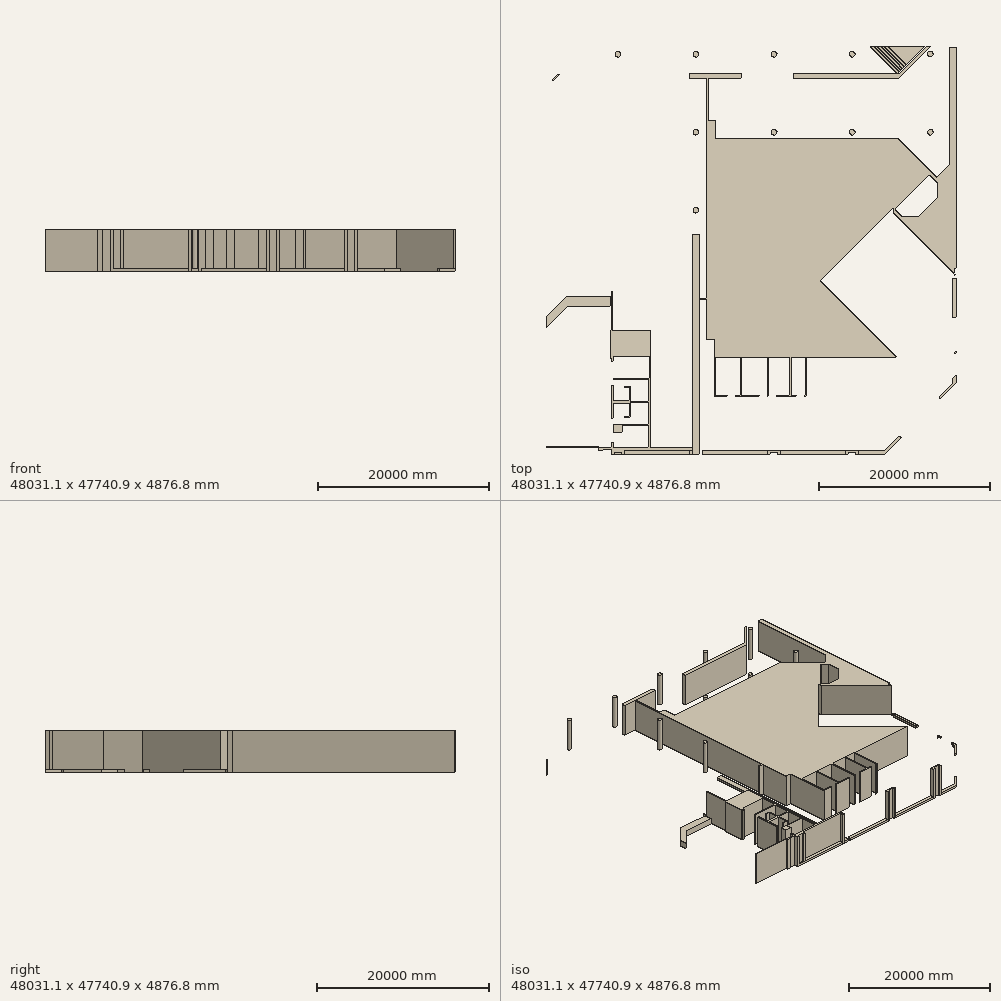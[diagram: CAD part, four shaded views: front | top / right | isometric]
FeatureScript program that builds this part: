
annotation { "Feature Type Name" : "Feature", "Feature Type Description" : "" }
export const myFeature = defineFeature(function(context is Context, id is Id, definition is map)
    precondition{}
    {
        {
            var Q0;
            Q0=qCreatedBy(makeId("Top.planeOp"),FACE);
            var sketch = newSketch(context, id + "F0", { "sketchPlane" : qUnion([Q0])});
            skPoint(sketch, "E0", {"position": v(-26.85, 4562) * mm});
            skPoint(sketch, "E1", {"position": v(-26.85, -4582) * mm});
            skLineSegment(sketch, "E2", {"start": v(-9950.22, -31763.64) * mm, "end": v(-9950.22, -33159.86) * mm});
            skLineSegment(sketch, "E3.bottom", {"start": v(-17558.31, -32264.25) * mm, "end": v(-11455.84, -32264.25) * mm});
            skLineSegment(sketch, "E3.top", {"start": v(-17558.31, -32382.5) * mm, "end": v(-11455.84, -32382.5) * mm});
            skLineSegment(sketch, "E3.left", {"start": v(-17558.31, -32264.25) * mm, "end": v(-17558.31, -32382.5) * mm});
            skLineSegment(sketch, "E3.right", {"start": v(-11455.84, -32264.25) * mm, "end": v(-11455.84, -32382.5) * mm});
            skLineSegment(sketch, "E4.bottom", {"start": v(-11455.84, -32382.5) * mm, "end": v(-10938.34, -32382.5) * mm});
            skLineSegment(sketch, "E4.top", {"start": v(-11455.84, -32680.38) * mm, "end": v(-10938.34, -32680.38) * mm});
            skLineSegment(sketch, "E4.left", {"start": v(-11455.84, -32382.5) * mm, "end": v(-11455.84, -32680.38) * mm});
            skLineSegment(sketch, "E4.right", {"start": v(-10938.34, -32382.5) * mm, "end": v(-10938.34, -32680.38) * mm});
            skLineSegment(sketch, "E5", {"start": v(-9950.22, -31763.64) * mm, "end": v(-9762.7, -31763.64) * mm});
            skLineSegment(sketch, "E6", {"start": v(-9762.7, -31763.64) * mm, "end": v(-9762.7, -32380.3) * mm});
            skLineSegment(sketch, "E7", {"start": v(-9762.7, -32380.3) * mm, "end": v(-5641.05, -32380.3) * mm});
            skLineSegment(sketch, "E8", {"start": v(-9950.22, -33159.86) * mm, "end": v(-9619.14, -33159.86) * mm});
            skLineSegment(sketch, "E9", {"start": v(-9619.14, -33159.86) * mm, "end": v(-9619.14, -32907.45) * mm});
            skLineSegment(sketch, "E10", {"start": v(-9619.14, -32907.45) * mm, "end": v(-8738.2, -32907.45) * mm});
            skLineSegment(sketch, "E11", {"start": v(-8738.2, -32907.45) * mm, "end": v(-8738.2, -33145.54) * mm});
            skLineSegment(sketch, "E12", {"start": v(-8738.2, -33145.54) * mm, "end": v(-8410.82, -33145.54) * mm});
            skLineSegment(sketch, "E13", {"start": v(-8410.82, -33145.54) * mm, "end": v(-8410.82, -32669.36) * mm});
            skLineSegment(sketch, "E14", {"start": v(-8410.82, -32669.36) * mm, "end": v(22197.76, -32669.36) * mm});
            skLineSegment(sketch, "E15", {"start": v(22197.76, -32669.36) * mm, "end": v(23797.54, -31074.11) * mm});
            skLineSegment(sketch, "E16", {"start": v(23797.54, -31074.11) * mm, "end": v(24012.82, -31290) * mm});
            skLineSegment(sketch, "E17", {"start": v(24012.82, -31290) * mm, "end": v(26211.2, -31290) * mm});
            skLineSegment(sketch, "E18", {"start": v(26211.2, -31290) * mm, "end": v(28592.14, -28914.34) * mm});
            skLineSegment(sketch, "E19", {"start": v(28592.14, -28914.34) * mm, "end": v(28592.14, -26694.78) * mm});
            skLineSegment(sketch, "E20", {"start": v(28592.14, -26694.78) * mm, "end": v(28388.32, -26490.39) * mm});
            skLineSegment(sketch, "E21", {"start": v(28388.32, -26490.39) * mm, "end": v(30000.29, -24882.99) * mm});
            skLineSegment(sketch, "E22", {"start": v(30000.29, -24882.99) * mm, "end": v(30000.29, -21715.72) * mm});
            skLineSegment(sketch, "E23", {"start": v(30000.29, -21715.72) * mm, "end": v(30471.14, -21715.72) * mm});
            skLineSegment(sketch, "E24", {"start": v(30471.14, -21715.72) * mm, "end": v(30471.14, -21395.8) * mm});
            skLineSegment(sketch, "E25", {"start": v(30471.14, -21395.8) * mm, "end": v(30212.23, -21395.8) * mm});
            skLineSegment(sketch, "E26", {"start": v(30212.23, -21395.8) * mm, "end": v(30212.23, -20478.92) * mm});
            skLineSegment(sketch, "E27", {"start": v(30212.23, -20478.92) * mm, "end": v(30471.14, -20478.92) * mm});
            skPoint(sketch, "E27.endSnap0", {"position": v(30471.14, -21555.76) * mm});
            skLineSegment(sketch, "E28", {"start": v(30471.14, -20478.92) * mm, "end": v(30471.14, -20162.3) * mm});
            skLineSegment(sketch, "E29", {"start": v(30471.14, -20162.3) * mm, "end": v(29991.03, -20162.3) * mm});
            skLineSegment(sketch, "E30", {"start": v(29991.03, -20162.3) * mm, "end": v(30000.29, -12570.11) * mm});
            skLineSegment(sketch, "E31", {"start": v(30000.29, -12570.11) * mm, "end": v(30453.57, -12570.67) * mm});
            skLineSegment(sketch, "E32", {"start": v(30453.57, -12570.67) * mm, "end": v(30453.57, -12236.58) * mm});
            skLineSegment(sketch, "E33", {"start": v(30453.57, -12236.58) * mm, "end": v(30215.9, -12236.58) * mm});
            skLineSegment(sketch, "E34", {"start": v(30215.9, -12236.58) * mm, "end": v(30215.9, -11358.68) * mm});
            skLineSegment(sketch, "E35", {"start": v(30215.9, -11358.68) * mm, "end": v(30472.75, -11358.68) * mm});
            skLineSegment(sketch, "E36", {"start": v(30472.75, -11358.68) * mm, "end": v(30472.75, 14474.16) * mm});
            skLineSegment(sketch, "E37", {"start": v(30472.75, 14474.16) * mm, "end": v(29691.03, 14474.16) * mm});
            skLineSegment(sketch, "E38", {"start": v(29691.03, 14474.16) * mm, "end": v(29691.03, 751.92) * mm});
            skLineSegment(sketch, "E39", {"start": v(29691.03, 751.92) * mm, "end": v(28176.9, -757.92) * mm});
            skLineSegment(sketch, "E40", {"start": v(28176.9, -757.92) * mm, "end": v(27421.13, 0) * mm});
            skLineSegment(sketch, "E41", {"start": v(23102.85, -4306.06) * mm, "end": v(14549.29, -12835.42) * mm});
            skLineSegment(sketch, "E42", {"start": v(23102.85, -4306.06) * mm, "end": v(23102.85, -4877.02) * mm});
            skLineSegment(sketch, "E43", {"start": v(23102.85, -4877.02) * mm, "end": v(36319.55, -18058.09) * mm});
            skLineSegment(sketch, "E44", {"start": v(36319.55, -18058.09) * mm, "end": v(22035.93, -32380.3) * mm});
            skLineSegment(sketch, "E45", {"start": v(23372.41, -4424.26) * mm, "end": v(23372.41, -4562.3) * mm});
            skLineSegment(sketch, "E46", {"start": v(23372.41, -4562.3) * mm, "end": v(24176.25, -5363.97) * mm});
            skLineSegment(sketch, "E47", {"start": v(24176.25, -5363.97) * mm, "end": v(26065.69, -5363.97) * mm});
            skLineSegment(sketch, "E48", {"start": v(26065.69, -5363.97) * mm, "end": v(28200.6, -3235.1) * mm});
            skLineSegment(sketch, "E49", {"start": v(28200.6, -3235.1) * mm, "end": v(28200.6, -1321.07) * mm});
            skLineSegment(sketch, "E50", {"start": v(28200.6, -1321.07) * mm, "end": v(27426.94, -545.21) * mm});
            skLineSegment(sketch, "E51", {"start": v(27426.94, -545.21) * mm, "end": v(27250.2, -545.21) * mm});
            skLineSegment(sketch, "E52", {"start": v(27250.2, -545.21) * mm, "end": v(23372.41, -4424.26) * mm});
            skLineSegment(sketch, "E53", {"start": v(27421.13, 0) * mm, "end": v(23591.37, 3840.63) * mm});
            skLineSegment(sketch, "E54", {"start": v(23591.37, 3840.63) * mm, "end": v(2272.8, 3840.63) * mm});
            skLineSegment(sketch, "E55", {"start": v(2272.8, 3840.63) * mm, "end": v(2272.8, 5998.23) * mm});
            skLineSegment(sketch, "E56", {"start": v(2272.8, 5998.23) * mm, "end": v(1416.9, 5998.23) * mm});
            skLineSegment(sketch, "E57", {"start": v(1416.9, 5998.23) * mm, "end": v(1416.9, 10830.47) * mm});
            skLineSegment(sketch, "E58", {"start": v(1416.9, 10830.47) * mm, "end": v(1221.14, 10830.47) * mm});
            skLineSegment(sketch, "E59", {"start": v(1221.14, 10830.47) * mm, "end": v(1221.14, -14864.76) * mm});
            skLineSegment(sketch, "E60", {"start": v(1221.14, -19710.1) * mm, "end": v(2272.8, -19710.1) * mm});
            skLineSegment(sketch, "E61", {"start": v(2114.71, -20733.64) * mm, "end": v(2114.71, -19710.1) * mm});
            skLineSegment(sketch, "E62", {"start": v(2114.71, -20733.64) * mm, "end": v(2114.71, -26433.55) * mm});
            skLineSegment(sketch, "E63", {"start": v(2114.71, -26433.55) * mm, "end": v(12953.96, -26433.55) * mm});
            skLineSegment(sketch, "E64", {"start": v(12953.96, -26433.55) * mm, "end": v(12953.96, -21846.23) * mm});
            skLineSegment(sketch, "E65", {"start": v(12953.96, -21846.23) * mm, "end": v(23534.6, -21846.23) * mm});
            skLineSegment(sketch, "E66", {"start": v(14549.29, -12835.42) * mm, "end": v(23534.6, -21846.23) * mm});
            skLineSegment(sketch, "E67.bottom", {"start": v(2270.48, -21826.68) * mm, "end": v(5186.94, -21826.68) * mm});
            skLineSegment(sketch, "E67.top", {"start": v(2270.48, -26267.02) * mm, "end": v(5186.94, -26267.02) * mm});
            skLineSegment(sketch, "E67.left", {"start": v(2270.48, -21826.68) * mm, "end": v(2270.48, -26267.02) * mm});
            skLineSegment(sketch, "E67.right", {"start": v(12795.42, -21826.68) * mm, "end": v(12795.42, -26267.02) * mm});
            skLineSegment(sketch, "E68", {"start": v(5186.94, -26267.02) * mm, "end": v(5186.94, -21826.68) * mm});
            skLineSegment(sketch, "E69", {"start": v(5332.87, -21826.68) * mm, "end": v(5332.87, -26267.02) * mm});
            skLineSegment(sketch, "E70", {"start": v(8282.63, -26267.02) * mm, "end": v(8282.63, -21826.68) * mm});
            skLineSegment(sketch, "E71", {"start": v(8448.12, -26267.02) * mm, "end": v(8448.12, -21826.68) * mm});
            skLineSegment(sketch, "E72", {"start": v(10967.35, -26267.02) * mm, "end": v(10967.35, -21826.68) * mm});
            skLineSegment(sketch, "E73", {"start": v(11142.18, -26267.02) * mm, "end": v(11142.18, -21826.68) * mm});
            skLineSegment(sketch, "E74.trimOffspring", {"start": v(5332.87, -26267.02) * mm, "end": v(8282.63, -26267.02) * mm});
            skLineSegment(sketch, "E75.trimOffspring", {"start": v(8448.12, -26267.02) * mm, "end": v(10967.35, -26267.02) * mm});
            skLineSegment(sketch, "E76.trimOffspring", {"start": v(11142.18, -26267.02) * mm, "end": v(12795.42, -26267.02) * mm});
            skLineSegment(sketch, "E77.trimOffspring", {"start": v(11142.18, -21826.68) * mm, "end": v(12795.42, -21826.68) * mm});
            skLineSegment(sketch, "E78.trimOffspring", {"start": v(8448.12, -21826.68) * mm, "end": v(10967.35, -21826.68) * mm});
            skLineSegment(sketch, "E79.trimOffspring", {"start": v(5332.87, -21826.68) * mm, "end": v(8282.63, -21826.68) * mm});
            skCircle(sketch, "E80", {"center": v(-26.85, -4582) * mm, "radius": 328.45 * mm});
            skCircle(sketch, "E81.0.1.0", {"center": v(-26.85, 4554.57) * mm, "radius": 328.45 * mm});
            skCircle(sketch, "E81.1.0.0", {"center": v(9121.68, -4582) * mm, "radius": 328.45 * mm});
            skCircle(sketch, "E81.1.1.0", {"center": v(9121.68, 4554.57) * mm, "radius": 328.45 * mm});
            skCircle(sketch, "E81.2.0.0", {"center": v(18270.2, -4582) * mm, "radius": 328.45 * mm});
            skCircle(sketch, "E81.2.1.0", {"center": v(18270.2, 4554.57) * mm, "radius": 328.45 * mm});
            skLineSegment(sketch, "E81.direction1", {"start": v(-26.85, -4582) * mm, "end": v(9121.68, -4582) * mm, "construction": true});
            skLineSegment(sketch, "E81.direction2", {"start": v(-26.85, -4582) * mm, "end": v(-26.85, 4554.57) * mm, "construction": true});
            skCircle(sketch, "E82.2.1.0", {"center": v(27432.52, 4548.8) * mm, "radius": 328.45 * mm});
            skCircle(sketch, "E83.0.0.2", {"center": v(-26.85, 13691.15) * mm, "radius": 328.45 * mm});
            skCircle(sketch, "E83.0.1.2", {"center": v(9121.68, 13691.15) * mm, "radius": 328.45 * mm});
            skCircle(sketch, "E83.0.2.2", {"center": v(18270.2, 13691.15) * mm, "radius": 328.45 * mm});
            skCircle(sketch, "E84.2.1.0", {"center": v(27415.87, 13708.97) * mm, "radius": 328.45 * mm});
            skCircle(sketch, "E85.0.0.2", {"center": v(-9163.03, 13691.68) * mm, "radius": 328.45 * mm});
            skCircle(sketch, "E86", {"center": v(-9163.03, -4581.46) * mm, "radius": 328.45 * mm});
            skLineSegment(sketch, "E87", {"start": v(-5368.57, -32380.3) * mm, "end": v(-5368.57, -18630.59) * mm});
            skLineSegment(sketch, "E88", {"start": v(-5368.57, -18630.59) * mm, "end": v(-9778.86, -18630.59) * mm});
            skLineSegment(sketch, "E89", {"start": v(-13716.14, -18630.59) * mm, "end": v(-17558.31, -22435.31) * mm});
            skLineSegment(sketch, "E90", {"start": v(-17558.31, -22435.31) * mm, "end": v(-17558.31, -22711.87) * mm});
            skLineSegment(sketch, "E91", {"start": v(-17558.31, -22711.87) * mm, "end": v(-16771.42, -21932.65) * mm});
            skLineSegment(sketch, "E92", {"start": v(-16771.42, -21932.65) * mm, "end": v(-9941.64, -21932.65) * mm});
            skLineSegment(sketch, "E93", {"start": v(-9941.64, -21932.65) * mm, "end": v(-9950.22, -31763.64) * mm});
            skLineSegment(sketch, "E94", {"start": v(-9762.7, -31763.64) * mm, "end": v(-9762.7, -27257.72) * mm});
            skLineSegment(sketch, "E95", {"start": v(-9762.7, -21738.5) * mm, "end": v(-5534.96, -21738.5) * mm});
            skLineSegment(sketch, "E96", {"start": v(-5534.96, -21738.5) * mm, "end": v(-5534.96, -24228.45) * mm});
            skLineSegment(sketch, "E97", {"start": v(-5534.96, -24228.45) * mm, "end": v(-9762.7, -24255.66) * mm});
            skLineSegment(sketch, "E98", {"start": v(-9762.7, -24422.07) * mm, "end": v(-5641.05, -24422.07) * mm});
            skLineSegment(sketch, "E99", {"start": v(-5641.05, -24422.07) * mm, "end": v(-5641.05, -26945.48) * mm});
            skLineSegment(sketch, "E100", {"start": v(-5641.05, -26945.48) * mm, "end": v(-7697.06, -26945.48) * mm});
            skLineSegment(sketch, "E101", {"start": v(-7697.06, -26945.48) * mm, "end": v(-7697.06, -25199.28) * mm});
            skLineSegment(sketch, "E102", {"start": v(-7697.06, -25199.28) * mm, "end": v(-9762.7, -25199.28) * mm});
            skLineSegment(sketch, "E103.bottom", {"start": v(-9762.7, -25341.58) * mm, "end": v(-7804.67, -25341.58) * mm});
            skLineSegment(sketch, "E103.top", {"start": v(-9762.7, -26805.34) * mm, "end": v(-7804.67, -26805.34) * mm});
            skLineSegment(sketch, "E103.left", {"start": v(-9762.7, -25341.58) * mm, "end": v(-9762.7, -26805.34) * mm});
            skLineSegment(sketch, "E103.right", {"start": v(-7804.67, -25341.58) * mm, "end": v(-7804.67, -26805.34) * mm});
            skLineSegment(sketch, "E104.bottom", {"start": v(-9762.7, -27257.72) * mm, "end": v(-7818.78, -27257.72) * mm});
            skLineSegment(sketch, "E104.top", {"start": v(-9762.7, -28712.38) * mm, "end": v(-7818.78, -28712.38) * mm});
            skLineSegment(sketch, "E104.left", {"start": v(-9762.7, -27257.72) * mm, "end": v(-9762.7, -28712.38) * mm});
            skLineSegment(sketch, "E104.right", {"start": v(-7818.78, -27257.72) * mm, "end": v(-7818.78, -28712.38) * mm});
            skLineSegment(sketch, "E105", {"start": v(-9762.7, -28854.12) * mm, "end": v(-7684.5, -28854.12) * mm});
            skLineSegment(sketch, "E106", {"start": v(-7684.5, -28854.12) * mm, "end": v(-7697.06, -27101.06) * mm});
            skLineSegment(sketch, "E107", {"start": v(-5641.05, -27101.06) * mm, "end": v(-5641.05, -29643.52) * mm});
            skLineSegment(sketch, "E108", {"start": v(-9762.7, -30572.31) * mm, "end": v(-8684, -30572.31) * mm});
            skLineSegment(sketch, "E109", {"start": v(-8684, -30572.31) * mm, "end": v(-8684, -29799.54) * mm});
            skLineSegment(sketch, "E110", {"start": v(-8684, -29799.54) * mm, "end": v(-5641.05, -29799.54) * mm});
            skLineSegment(sketch, "E111.trimOffspring", {"start": v(-5368.57, -32380.3) * mm, "end": v(22035.93, -32380.3) * mm});
            skLineSegment(sketch, "E112", {"start": v(-5641.05, -29643.52) * mm, "end": v(-9762.7, -29643.52) * mm});
            skLineSegment(sketch, "E113.trimOffspring", {"start": v(-5641.05, -29799.54) * mm, "end": v(-5641.05, -32380.3) * mm});
            skLineSegment(sketch, "E114.trimOffspring", {"start": v(-9762.7, -26805.34) * mm, "end": v(-9762.7, -21738.5) * mm});
            skLineSegment(sketch, "E115", {"start": v(-9938.81, 3812.34) * mm, "end": v(-9938.81, 6704.85) * mm});
            skLineSegment(sketch, "E116", {"start": v(-9938.81, 6704.85) * mm, "end": v(-13683.46, 6704.85) * mm});
            skLineSegment(sketch, "E117", {"start": v(-13683.46, 6704.85) * mm, "end": v(-15867.48, 4542.12) * mm});
            skLineSegment(sketch, "E118", {"start": v(-15867.48, 4542.12) * mm, "end": v(-15867.48, 3814.12) * mm});
            skLineSegment(sketch, "E119", {"start": v(-15867.48, 3814.12) * mm, "end": v(-9938.81, 3812.34) * mm});
            skLineSegment(sketch, "E120.bottom", {"start": v(-9681.28, 6600.56) * mm, "end": v(-7756.34, 6600.56) * mm});
            skLineSegment(sketch, "E120.top", {"start": v(-9681.28, 4073.02) * mm, "end": v(-7756.34, 4073.02) * mm});
            skLineSegment(sketch, "E120.left", {"start": v(-9681.28, 6600.56) * mm, "end": v(-9681.28, 4073.02) * mm});
            skLineSegment(sketch, "E120.right", {"start": v(-7756.34, 6600.56) * mm, "end": v(-7756.34, 4073.02) * mm});
            skLineSegment(sketch, "E121.right", {"start": v(-5588.68, 6592.19) * mm, "end": v(-5588.68, 4064.65) * mm});
            skLineSegment(sketch, "E121.left", {"start": v(-7513.63, 6592.19) * mm, "end": v(-7513.63, 4064.65) * mm});
            skLineSegment(sketch, "E121.top", {"start": v(-7513.63, 4064.65) * mm, "end": v(-5588.68, 4064.65) * mm});
            skLineSegment(sketch, "E121.bottom", {"start": v(-7513.63, 6592.19) * mm, "end": v(-5588.68, 6592.19) * mm});
            skLineSegment(sketch, "E122", {"start": v(-9938.81, -14647.96) * mm, "end": v(-9938.81, 8173.67) * mm});
            skLineSegment(sketch, "E123", {"start": v(-9938.81, -14647.96) * mm, "end": v(-9778.86, -14647.96) * mm});
            skLineSegment(sketch, "E124", {"start": v(-9778.86, -14647.96) * mm, "end": v(-9778.86, -14864.76) * mm});
            skLineSegment(sketch, "E125", {"start": v(-9778.86, -14864.76) * mm, "end": v(1221.14, -14864.76) * mm});
            skLineSegment(sketch, "E126", {"start": v(1221.14, -15049.13) * mm, "end": v(-9778.86, -15049.13) * mm});
            skLineSegment(sketch, "E127", {"start": v(-9778.86, 8173.67) * mm, "end": v(-9778.86, -15049.13) * mm});
            skLineSegment(sketch, "E128.trimOffspring", {"start": v(1221.14, -15049.13) * mm, "end": v(1221.14, -19710.1) * mm});
            skLineSegment(sketch, "E129", {"start": v(-9938.81, -14647.96) * mm, "end": v(-15154.65, -14647.96) * mm});
            skLineSegment(sketch, "E130", {"start": v(-15154.65, -14647.96) * mm, "end": v(-17558.31, -17028.2) * mm});
            skLineSegment(sketch, "E131", {"start": v(-17558.31, -17028.2) * mm, "end": v(-17558.31, -18375.53) * mm});
            skLineSegment(sketch, "E132", {"start": v(-17558.31, -18375.53) * mm, "end": v(-14995.76, -15837.96) * mm});
            skLineSegment(sketch, "E133", {"start": v(-14995.76, -15837.96) * mm, "end": v(-9938.81, -15837.96) * mm});
            skLineSegment(sketch, "E134", {"start": v(-9938.81, 8173.67) * mm, "end": v(-9938.81, -18630.59) * mm});
            skLineSegment(sketch, "E135", {"start": v(-9778.86, 8173.67) * mm, "end": v(-9778.86, -18630.59) * mm});
            skLineSegment(sketch, "E136.trimOffspring", {"start": v(-9938.81, -18630.59) * mm, "end": v(-13716.14, -18630.59) * mm});
            skLineSegment(sketch, "E137", {"start": v(-16854.94, 10671.88) * mm, "end": v(-16764.56, 10580.6) * mm});
            skLineSegment(sketch, "E138", {"start": v(-16854.94, 10671.88) * mm, "end": v(-16165.11, 11354.98) * mm});
            skLineSegment(sketch, "E139", {"start": v(-16165.11, 11354.98) * mm, "end": v(-16074.73, 11263.71) * mm});
            skLineSegment(sketch, "E140", {"start": v(-16764.56, 10580.6) * mm, "end": v(-16074.73, 11263.71) * mm});
            skLineSegment(sketch, "E141", {"start": v(1221.14, 10830.47) * mm, "end": v(-798.64, 10830.47) * mm});
            skLineSegment(sketch, "E142", {"start": v(-798.64, 10830.47) * mm, "end": v(-798.64, 11424.72) * mm});
            skLineSegment(sketch, "E143", {"start": v(-798.64, 11424.72) * mm, "end": v(5292.94, 11424.72) * mm});
            skLineSegment(sketch, "E144", {"start": v(5292.94, 11424.72) * mm, "end": v(5292.94, 10830.47) * mm});
            skLineSegment(sketch, "E145", {"start": v(5292.94, 10830.47) * mm, "end": v(1416.9, 10830.47) * mm});
            skLineSegment(sketch, "E146", {"start": v(11396.94, 11424.72) * mm, "end": v(23811.16, 11424.72) * mm});
            skLineSegment(sketch, "E147", {"start": v(23811.16, 11424.72) * mm, "end": v(26998.76, 14581.05) * mm});
            skLineSegment(sketch, "E148", {"start": v(11396.94, 11424.72) * mm, "end": v(11396.94, 10830.47) * mm});
            skLineSegment(sketch, "E149", {"start": v(11396.94, 10830.47) * mm, "end": v(23674.7, 10830.47) * mm});
            skLineSegment(sketch, "E150", {"start": v(23674.7, 10830.47) * mm, "end": v(27462.44, 14581.05) * mm});
            skLineSegment(sketch, "E151.bottom", {"start": v(12953.96, -21846.23) * mm, "end": v(13730.82, -21846.23) * mm});
            skLineSegment(sketch, "E151.top", {"start": v(12953.96, -25034.62) * mm, "end": v(13730.82, -25034.62) * mm});
            skLineSegment(sketch, "E151.left", {"start": v(12953.96, -21846.23) * mm, "end": v(12953.96, -25034.62) * mm});
            skLineSegment(sketch, "E151.right", {"start": v(13730.82, -21846.23) * mm, "end": v(13730.82, -25034.62) * mm});
            skLineSegment(sketch, "E152.bottom", {"start": v(-8397.25, -14864.76) * mm, "end": v(-798.64, -14864.76) * mm});
            skLineSegment(sketch, "E152.top", {"start": v(-8397.25, 11424.72) * mm, "end": v(-798.64, 11424.72) * mm});
            skLineSegment(sketch, "E152.left", {"start": v(-8397.25, -14864.76) * mm, "end": v(-8397.25, 11424.72) * mm});
            skLineSegment(sketch, "E152.right", {"start": v(-798.64, -14864.76) * mm, "end": v(-798.64, 11424.72) * mm});
            skLineSegment(sketch, "E153.bottom", {"start": v(-11468.9, -14075.92) * mm, "end": v(-8397.25, -14075.92) * mm});
            skLineSegment(sketch, "E153.top", {"start": v(-11468.9, -14666.65) * mm, "end": v(-8397.25, -14666.65) * mm});
            skLineSegment(sketch, "E153.left", {"start": v(-11468.9, -14075.92) * mm, "end": v(-11468.9, -14666.65) * mm});
            skLineSegment(sketch, "E153.right", {"start": v(-8397.25, -14075.92) * mm, "end": v(-8397.25, -14666.65) * mm});
            skLineSegment(sketch, "E154.1.0.0", {"start": v(-806.22, -33159.86) * mm, "end": v(-475.14, -33159.86) * mm});
            skLineSegment(sketch, "E154.2.0.0", {"start": v(8337.78, -33159.86) * mm, "end": v(8668.86, -33159.86) * mm});
            skLineSegment(sketch, "E154.2.0.1", {"start": v(8668.86, -32907.45) * mm, "end": v(9549.8, -32907.45) * mm});
            skLineSegment(sketch, "E154.2.0.2", {"start": v(9549.8, -32907.45) * mm, "end": v(9549.8, -33159.86) * mm});
            skLineSegment(sketch, "E154.2.0.3", {"start": v(9877.18, -33159.86) * mm, "end": v(9877.18, -32669.36) * mm});
            skLineSegment(sketch, "E154.3.0.0", {"start": v(17481.78, -33159.86) * mm, "end": v(17812.86, -33159.86) * mm});
            skLineSegment(sketch, "E154.3.0.1", {"start": v(17812.86, -32907.45) * mm, "end": v(18693.8, -32907.45) * mm});
            skLineSegment(sketch, "E154.3.0.2", {"start": v(18693.8, -32907.45) * mm, "end": v(18693.8, -33145.54) * mm});
            skLineSegment(sketch, "E154.3.0.3", {"start": v(19021.18, -33159.86) * mm, "end": v(19021.18, -32669.36) * mm});
            skLineSegment(sketch, "E154.direction1", {"start": v(-9950.22, -33159.86) * mm, "end": v(-806.22, -33159.86) * mm, "construction": true});
            skLineSegment(sketch, "E155", {"start": v(17481.78, -33159.86) * mm, "end": v(17481.78, -32669.36) * mm});
            skLineSegment(sketch, "E156", {"start": v(-806.22, -33159.86) * mm, "end": v(-806.22, -32669.36) * mm});
            skLineSegment(sketch, "E157", {"start": v(-9950.22, -33159.86) * mm, "end": v(22137.66, -33159.86) * mm});
            skLineSegment(sketch, "E158", {"start": v(24012.82, -31290) * mm, "end": v(22137.66, -33159.86) * mm});
            skLineSegment(sketch, "E159", {"start": v(28592.14, -26694.78) * mm, "end": v(30463.91, -24828.3) * mm});
            skLineSegment(sketch, "E160", {"start": v(30471.14, -21715.72) * mm, "end": v(30463.91, -24828.3) * mm});
            skLineSegment(sketch, "E161", {"start": v(30471.14, -21715.72) * mm, "end": v(30471.7, -18087.35) * mm});
            skLineSegment(sketch, "E162", {"start": v(29994.73, -17133.52) * mm, "end": v(30471.85, -17134.1) * mm});
            skLineSegment(sketch, "E163", {"start": v(29993.56, -18086.77) * mm, "end": v(30471.7, -18087.35) * mm});
            skLineSegment(sketch, "E164.trimOffspring", {"start": v(30471.85, -17134.1) * mm, "end": v(30472.75, -11358.68) * mm});
            skLineSegment(sketch, "E165", {"start": v(-10938.34, -32382.5) * mm, "end": v(-9950.22, -32382.5) * mm});
            skLineSegment(sketch, "E166", {"start": v(-10938.34, -32550.92) * mm, "end": v(-9950.22, -32550.92) * mm});
            skLineSegment(sketch, "E167", {"start": v(3611.54, -26267.02) * mm, "end": v(3611.54, -26433.55) * mm});
            skLineSegment(sketch, "E168", {"start": v(4527.36, -26267.02) * mm, "end": v(4527.36, -26433.55) * mm});
            skLineSegment(sketch, "E169", {"start": v(7342.54, -26267.02) * mm, "end": v(7342.54, -26433.55) * mm});
            skLineSegment(sketch, "E170", {"start": v(8282.63, -26267.02) * mm, "end": v(8282.63, -26433.55) * mm});
            skLineSegment(sketch, "E171", {"start": v(8448.12, -26267.02) * mm, "end": v(8448.12, -26433.55) * mm});
            skLineSegment(sketch, "E172", {"start": v(9387.34, -26267.02) * mm, "end": v(9387.34, -26433.55) * mm});
            skLineSegment(sketch, "E173", {"start": v(11770.41, -26433.55) * mm, "end": v(11770.41, -26267.02) * mm});
            skLineSegment(sketch, "E174", {"start": v(12655.65, -26267.02) * mm, "end": v(12655.65, -26433.55) * mm});
            skLineSegment(sketch, "E175", {"start": v(2114.71, -20655.1) * mm, "end": v(2272.8, -20655.1) * mm});
            skLineSegment(sketch, "E176", {"start": v(28200.6, -2802.8) * mm, "end": v(28399.68, -2802.8) * mm});
            skLineSegment(sketch, "E177", {"start": v(28399.68, -2802.8) * mm, "end": v(28395.17, -2721.45) * mm});
            skLineSegment(sketch, "E178", {"start": v(28395.17, -2721.45) * mm, "end": v(28592.14, -2721.45) * mm});
            skLineSegment(sketch, "E179", {"start": v(28592.14, -1862.71) * mm, "end": v(28395.17, -1862.71) * mm});
            skLineSegment(sketch, "E180", {"start": v(28395.17, -1862.71) * mm, "end": v(28395.17, -1803.95) * mm});
            skLineSegment(sketch, "E181", {"start": v(28395.17, -1803.95) * mm, "end": v(28200.82, -1803.95) * mm});
            skLineSegment(sketch, "E182", {"start": v(-9762.7, -30646.07) * mm, "end": v(-9949.24, -30645.9) * mm});
            skLineSegment(sketch, "E183", {"start": v(-9762.7, -29551.22) * mm, "end": v(-9948.29, -29551.06) * mm});
            skLineSegment(sketch, "E184", {"start": v(-9762.7, -28961.95) * mm, "end": v(-9947.77, -28961.95) * mm});
            skLineSegment(sketch, "E185", {"start": v(-9177.87, -28712.38) * mm, "end": v(-9177.87, -28854.12) * mm});
            skLineSegment(sketch, "E186", {"start": v(-8473.27, -28707.53) * mm, "end": v(-8473.27, -28854.12) * mm});
            skLineSegment(sketch, "E187", {"start": v(-7697.06, -27101.06) * mm, "end": v(-5641.05, -27101.06) * mm});
            skPoint(sketch, "E188.orphan", {"position": v(-5641.05, -27086.34) * mm});
            skLineSegment(sketch, "E189", {"start": v(-6705.31, -27101.06) * mm, "end": v(-6705.31, -27707.33) * mm});
            skLineSegment(sketch, "E190", {"start": v(-6705.31, -27707.33) * mm, "end": v(-5641.05, -27707.33) * mm});
            skLineSegment(sketch, "E191", {"start": v(-9180.75, -25341.58) * mm, "end": v(-9180.75, -25199.28) * mm});
            skLineSegment(sketch, "E192", {"start": v(-8474.8, -25341.58) * mm, "end": v(-8474.8, -25199.28) * mm});
            skLineSegment(sketch, "E193", {"start": v(-9944.4, -25087.62) * mm, "end": v(-9762.7, -25087.77) * mm});
            skLineSegment(sketch, "E194", {"start": v(-9944.96, -24505.03) * mm, "end": v(-9762.7, -24505.03) * mm});
            skLineSegment(sketch, "E195", {"start": v(-9763.33, -24134.92) * mm, "end": v(-9943.56, -24134.76) * mm});
            skLineSegment(sketch, "E196", {"start": v(-9941.98, -22319.58) * mm, "end": v(-9762.7, -22319.74) * mm});
            skLineSegment(sketch, "E197", {"start": v(-10073.08, -21932.65) * mm, "end": v(-10073.08, 3812.38) * mm});
            skLineSegment(sketch, "E198", {"start": v(-11216.54, 3812.73) * mm, "end": v(-11216.55, 3786.54) * mm});
            skLineSegment(sketch, "E199", {"start": v(-11216.55, 3786.54) * mm, "end": v(-11168.09, 3786.53) * mm});
            skLineSegment(sketch, "E200", {"start": v(-11168.09, 3786.53) * mm, "end": v(-11168.09, 3635.32) * mm});
            skLineSegment(sketch, "E201", {"start": v(-11168.09, 3635.32) * mm, "end": v(-11216.55, 3635.32) * mm});
            skLineSegment(sketch, "E202", {"start": v(-11216.72, -21859.56) * mm, "end": v(-11216.72, -21932.65) * mm});
            skLineSegment(sketch, "E203", {"start": v(39465.43, -12078.48) * mm, "end": v(26593.58, -24913.9) * mm});
            skLineSegment(sketch, "E204", {"start": v(40125.37, -12740.3) * mm, "end": v(27253.52, -25575.7) * mm});
            skLineSegment(sketch, "E205", {"start": v(23591.98, 11424.72) * mm, "end": v(23773.15, 11604.12) * mm});
            skLineSegment(sketch, "E206", {"start": v(23773.15, 11604.12) * mm, "end": v(20825.43, 14581.05) * mm});
            skLineSegment(sketch, "E207", {"start": v(20825.43, 14581.05) * mm, "end": v(20380.94, 14581.05) * mm});
            skLineSegment(sketch, "E208", {"start": v(20380.94, 14581.05) * mm, "end": v(23506.3, 11424.72) * mm});
            skLineSegment(sketch, "E209", {"start": v(23506.3, 11424.72) * mm, "end": v(23597.54, 11423.58) * mm});
            skLineSegment(sketch, "E210", {"start": v(23771.43, 11604.16) * mm, "end": v(23979.95, 11810.64) * mm});
            skLineSegment(sketch, "E211", {"start": v(23979.95, 11810.64) * mm, "end": v(21236.73, 14581.05) * mm});
            skLineSegment(sketch, "E212", {"start": v(21236.73, 14581.05) * mm, "end": v(21619.19, 14581.05) * mm});
            skLineSegment(sketch, "E213", {"start": v(21619.19, 14581.05) * mm, "end": v(24170.81, 12004.14) * mm});
            skLineSegment(sketch, "E214", {"start": v(23974.54, 11809.78) * mm, "end": v(24593.34, 12422.52) * mm});
            skLineSegment(sketch, "E215", {"start": v(24390.62, 12221.66) * mm, "end": v(22054.38, 14581.05) * mm});
            skLineSegment(sketch, "E216", {"start": v(22054.38, 14581.05) * mm, "end": v(21619.19, 14581.05) * mm});
            skLineSegment(sketch, "E217", {"start": v(22054.38, 14581.05) * mm, "end": v(22442.31, 14581.05) * mm});
            skLineSegment(sketch, "E218", {"start": v(22442.31, 14581.05) * mm, "end": v(24593.34, 12422.52) * mm});
            skLineSegment(sketch, "E219", {"start": v(24593.34, 12422.52) * mm, "end": v(26759.4, 14581.05) * mm});
            skLineSegment(sketch, "E220", {"start": v(26759.4, 14581.05) * mm, "end": v(22442.31, 14581.05) * mm});
            skLineSegment(sketch, "E221", {"start": v(20825.43, 14581.05) * mm, "end": v(21236.73, 14581.05) * mm});
            skLineSegment(sketch, "E222", {"start": v(26998.76, 14581.05) * mm, "end": v(27462.44, 14581.05) * mm});
            skLineSegment(sketch, "E223", {"start": v(-475.14, -33159.86) * mm, "end": v(-475.14, -7412.4) * mm});
            skLineSegment(sketch, "E224", {"start": v(-475.14, -7412.4) * mm, "end": v(403.24, -7412.4) * mm});
            skLineSegment(sketch, "E225", {"start": v(403.24, -7412.4) * mm, "end": v(403.24, -33159.86) * mm});
            skLineSegment(sketch, "E226", {"start": v(403.24, -33159.86) * mm, "end": v(737.83, -33159.86) * mm});
            skLineSegment(sketch, "E227", {"start": v(737.83, -33159.86) * mm, "end": v(737.83, -32669.36) * mm});
            skPoint(sketch, "E228.orphan", {"position": v(9877.18, -33145.54) * mm});
            skPoint(sketch, "E229.orphan", {"position": v(9549.8, -33145.54) * mm});
            skLineSegment(sketch, "E230", {"start": v(8668.86, -32907.45) * mm, "end": v(8668.86, -33159.86) * mm});
            skLineSegment(sketch, "E231", {"start": v(8337.78, -33159.86) * mm, "end": v(8337.78, -32669.36) * mm});
            skPoint(sketch, "E232.orphan", {"position": v(19021.18, -33145.54) * mm});
            skLineSegment(sketch, "E233", {"start": v(18693.8, -33145.54) * mm, "end": v(18693.8, -33159.86) * mm});
            skLineSegment(sketch, "E234", {"start": v(17812.86, -32907.45) * mm, "end": v(17816.75, -33159.86) * mm});
            skSolve(sketch);
        }
        {
            var Q0;
            {var subQ57=sQuery(id+"F0.wireOp",EDGE,"E5");Q0=makeQuery(id+"F0.imprint","IMPRINT",FACE,{"disambiguationData":[TD([[makeQuery(id+"F0.imprint","IMPRINT",EDGE,{"derivedFrom":subQ57}),-1.0]])]});}
            var Q1;
            {var subQ18=sQuery(id+"F0.wireOp",EDGE,"E54");Q1=makeQuery(id+"F0.imprint","IMPRINT",FACE,{"disambiguationData":[TD([[makeQuery(id+"F0.imprint","IMPRINT",EDGE,{"derivedFrom":subQ18}),1.0]])]});}
            var Q2;
            Q2=makeQuery(id+"F0.imprint","IMPRINT",FACE,{"disambiguationData":[TD([[makeQuery(id+"F0.imprint","IMPRINT",EDGE,{"derivedFrom":sQuery(id+"F0.wireOp",EDGE,"E81.0.1.0")}),1.0]])]});
            var Q3;
            Q3=makeQuery(id+"F0.imprint","IMPRINT",FACE,{"disambiguationData":[TD([[makeQuery(id+"F0.imprint","IMPRINT",EDGE,{"derivedFrom":sQuery(id+"F0.wireOp",EDGE,"E80")}),1.0]])]});
            var Q4;
            Q4=makeQuery(id+"F0.imprint","IMPRINT",FACE,{"disambiguationData":[TD([[makeQuery(id+"F0.imprint","IMPRINT",EDGE,{"derivedFrom":sQuery(id+"F0.wireOp",EDGE,"E81.1.0.0")}),1.0]])]});
            var Q5;
            Q5=makeQuery(id+"F0.imprint","IMPRINT",FACE,{"disambiguationData":[TD([[makeQuery(id+"F0.imprint","IMPRINT",EDGE,{"derivedFrom":sQuery(id+"F0.wireOp",EDGE,"E81.2.0.0")}),1.0]])]});
            var Q6;
            Q6=makeQuery(id+"F0.imprint","IMPRINT",FACE,{"disambiguationData":[TD([[makeQuery(id+"F0.imprint","IMPRINT",EDGE,{"derivedFrom":sQuery(id+"F0.wireOp",EDGE,"E85.0.0.2")}),1.0]])]});
            var Q7;
            Q7=makeQuery(id+"F0.imprint","IMPRINT",FACE,{"disambiguationData":[TD([[makeQuery(id+"F0.imprint","IMPRINT",EDGE,{"derivedFrom":sQuery(id+"F0.wireOp",EDGE,"E83.0.0.2")}),1.0]])]});
            var Q8;
            Q8=makeQuery(id+"F0.imprint","IMPRINT",FACE,{"disambiguationData":[TD([[makeQuery(id+"F0.imprint","IMPRINT",EDGE,{"derivedFrom":sQuery(id+"F0.wireOp",EDGE,"E81.1.1.0")}),1.0]])]});
            var Q9;
            Q9=makeQuery(id+"F0.imprint","IMPRINT",FACE,{"disambiguationData":[TD([[makeQuery(id+"F0.imprint","IMPRINT",EDGE,{"derivedFrom":sQuery(id+"F0.wireOp",EDGE,"E83.0.1.2")}),1.0]])]});
            var Q10;
            Q10=makeQuery(id+"F0.imprint","IMPRINT",FACE,{"disambiguationData":[TD([[makeQuery(id+"F0.imprint","IMPRINT",EDGE,{"derivedFrom":sQuery(id+"F0.wireOp",EDGE,"E83.0.2.2")}),1.0]])]});
            var Q11;
            Q11=makeQuery(id+"F0.imprint","IMPRINT",FACE,{"disambiguationData":[TD([[makeQuery(id+"F0.imprint","IMPRINT",EDGE,{"derivedFrom":sQuery(id+"F0.wireOp",EDGE,"E81.2.1.0")}),1.0]])]});
            var Q12;
            Q12=makeQuery(id+"F0.imprint","IMPRINT",FACE,{"disambiguationData":[TD([[makeQuery(id+"F0.imprint","IMPRINT",EDGE,{"derivedFrom":sQuery(id+"F0.wireOp",EDGE,"E82.2.1.0")}),1.0]])]});
            var Q13;
            Q13=makeQuery(id+"F0.imprint","IMPRINT",FACE,{"disambiguationData":[TD([[makeQuery(id+"F0.imprint","IMPRINT",EDGE,{"derivedFrom":sQuery(id+"F0.wireOp",EDGE,"E84.2.1.0")}),1.0]])]});
            var Q14;
            {var subQ3=sQuery(id+"F0.wireOp",EDGE,"E4.bottom");Q14=makeQuery(id+"F0.imprint","IMPRINT",FACE,{"disambiguationData":[TD([[makeQuery(id+"F0.imprint","IMPRINT",EDGE,{"derivedFrom":subQ3}),-1.0]])]});}
            var Q15;
            {var subQ2=sQuery(id+"F0.wireOp",EDGE,"E165");Q15=makeQuery(id+"F0.imprint","IMPRINT",FACE,{"disambiguationData":[TD([[makeQuery(id+"F0.imprint","IMPRINT",EDGE,{"derivedFrom":subQ2}),-1.0]])]});}
            var Q16;
            Q16=makeQuery(id+"F0.imprint","IMPRINT",FACE,{"disambiguationData":[TD([[makeQuery(id+"F0.imprint","IMPRINT",EDGE,{"derivedFrom":sQuery(id+"F0.wireOp",EDGE,"E3.bottom")}),-1.0]])]});
            var Q17;
            {var subQ4=sQuery(id+"F0.wireOp",EDGE,"E147");Q17=makeQuery(id+"F0.imprint","IMPRINT",FACE,{"disambiguationData":[TD([[makeQuery(id+"F0.imprint","IMPRINT",EDGE,{"derivedFrom":subQ4}),-1.0]])]});}
            var Q18;
            Q18=makeQuery(id+"F0.imprint","IMPRINT",FACE,{"disambiguationData":[TD([[makeQuery(id+"F0.imprint","IMPRINT",EDGE,{"derivedFrom":sQuery(id+"F0.wireOp",EDGE,"E58")}),-1.0]])]});
            extrude(context, id + "F1", {"entities" : qUnion([Q0, Q1, Q2, Q3, Q4, Q5, Q6, Q7, Q8, Q9, Q10, Q11, Q12, Q13, Q14, Q15, Q16, Q17, Q18]), "depth" : 4876.8 * mm});
        }
        {
            var Q0;
            {var subQ6=sQuery(id+"F0.wireOp",EDGE,"E130");Q0=makeQuery(id+"F0.imprint","IMPRINT",FACE,{"disambiguationData":[TD([[makeQuery(id+"F0.imprint","IMPRINT",EDGE,{"derivedFrom":subQ6}),1.0]])]});}
            var Q1;
            {var subQ2=sQuery(id+"F0.wireOp",EDGE,"E152.bottom");Q1=makeQuery(id+"F0.imprint","IMPRINT",FACE,{"disambiguationData":[TD([[makeQuery(id+"F0.imprint","IMPRINT",EDGE,{"derivedFrom":subQ2}),1.0]])]});}
            var Q2;
            {var subQ4=sQuery(id+"F0.wireOp",EDGE,"E123");Q2=makeQuery(id+"F0.imprint","IMPRINT",FACE,{"disambiguationData":[TD([[makeQuery(id+"F0.imprint","IMPRINT",EDGE,{"derivedFrom":subQ4}),1.0]])]});}
            var Q3;
            Q3=makeQuery(id+"F0.imprint","IMPRINT",FACE,{"disambiguationData":[TD([[makeQuery(id+"F0.imprint","IMPRINT",EDGE,{"derivedFrom":sQuery(id+"F0.wireOp",EDGE,"E151.bottom")}),-1.0]])]});
            extrude(context, id + "F2", {"entities" : qUnion([Q0, Q1, Q2, Q3]), "depth" : 914.4 * mm});
        }
        {
            var Q0;
            {var subQ3=sQuery(id+"F0.wireOp",EDGE,"E205");Q0=makeQuery(id+"F0.imprint","IMPRINT",FACE,{"disambiguationData":[TD([[makeQuery(id+"F0.imprint","IMPRINT",EDGE,{"derivedFrom":subQ3}),1.0]])]});}
            extrude(context, id + "F3", {"entities" : qUnion([Q0]), "operationType" : NewBodyOperationType.ADD, "depth" : 177.8 * mm});
        }
        {
            var Q0;
            {var subQ0=sQuery(id+"F0.wireOp",EDGE,"E221");Q0=makeQuery(id+"F0.imprint","IMPRINT",FACE,{"disambiguationData":[TD([[makeQuery(id+"F0.imprint","IMPRINT",EDGE,{"derivedFrom":subQ0}),-1.0]])]});}
            extrude(context, id + "F4", {"entities" : qUnion([Q0]), "operationType" : NewBodyOperationType.ADD, "depth" : 355.6 * mm});
        }
        {
            var Q0;
            {var subQ4=sQuery(id+"F0.wireOp",EDGE,"E212");Q0=makeQuery(id+"F0.imprint","IMPRINT",FACE,{"disambiguationData":[TD([[makeQuery(id+"F0.imprint","IMPRINT",EDGE,{"derivedFrom":subQ4}),-1.0]])]});}
            extrude(context, id + "F5", {"entities" : qUnion([Q0]), "operationType" : NewBodyOperationType.ADD, "depth" : 533.4 * mm});
        }
        {
            var Q0;
            {var subQ4=sQuery(id+"F0.wireOp",EDGE,"E213");Q0=makeQuery(id+"F0.imprint","IMPRINT",FACE,{"disambiguationData":[TD([[makeQuery(id+"F0.imprint","IMPRINT",EDGE,{"derivedFrom":subQ4}),1.0]])]});}
            extrude(context, id + "F6", {"entities" : qUnion([Q0]), "operationType" : NewBodyOperationType.ADD, "depth" : 711.2 * mm});
        }
        {
            var Q0;
            {var subQ1=sQuery(id+"F0.wireOp",EDGE,"E217");Q0=makeQuery(id+"F0.imprint","IMPRINT",FACE,{"disambiguationData":[TD([[makeQuery(id+"F0.imprint","IMPRINT",EDGE,{"derivedFrom":subQ1}),-1.0]])]});}
            extrude(context, id + "F7", {"entities" : qUnion([Q0]), "operationType" : NewBodyOperationType.ADD, "depth" : 889 * mm});
        }
        {
            var Q0;
            Q0=makeQuery(id+"F0.imprint","IMPRINT",FACE,{"disambiguationData":[TD([[makeQuery(id+"F0.imprint","IMPRINT",EDGE,{"derivedFrom":sQuery(id+"F0.wireOp",EDGE,"E218")}),1.0]])]});
            extrude(context, id + "F8", {"entities" : qUnion([Q0]), "operationType" : NewBodyOperationType.ADD, "depth" : 1066.8 * mm});
        }
        {
            var Q0;
            Q0=makeQuery(id+"F0.imprint","IMPRINT",FACE,{"disambiguationData":[TD([[makeQuery(id+"F0.imprint","IMPRINT",EDGE,{"derivedFrom":sQuery(id+"F0.wireOp",EDGE,"E137")}),1.0]])]});
            extrude(context, id + "F9", {"entities" : qUnion([Q0]), "depth" : 2133.6 * mm});
        }
        {
            var Q0;
            {var subQ3=sQuery(id+"F0.wireOp",EDGE,"E9");Q0=makeQuery(id+"F0.imprint","IMPRINT",FACE,{"disambiguationData":[TD([[makeQuery(id+"F0.imprint","IMPRINT",EDGE,{"derivedFrom":subQ3}),-1.0]])]});}
            var Q1;
            {var subQ1=sQuery(id+"F0.wireOp",EDGE,"E223");Q1=makeQuery(id+"F0.imprint","IMPRINT",FACE,{"disambiguationData":[TD([[makeQuery(id+"F0.imprint","IMPRINT",EDGE,{"derivedFrom":subQ1}),-1.0]])]});}
            var Q2;
            {var subQ3=sQuery(id+"F0.wireOp",EDGE,"E155");Q2=makeQuery(id+"F0.imprint","IMPRINT",FACE,{"disambiguationData":[TD([[makeQuery(id+"F0.imprint","IMPRINT",EDGE,{"derivedFrom":subQ3}),1.0]])]});}
            var Q3;
            {var subQ4=sQuery(id+"F0.wireOp",EDGE,"E15");Q3=makeQuery(id+"F0.imprint","IMPRINT",FACE,{"disambiguationData":[TD([[makeQuery(id+"F0.imprint","IMPRINT",EDGE,{"derivedFrom":subQ4}),-1.0]])]});}
            var Q4;
            Q4=makeQuery(id+"F0.imprint","IMPRINT",FACE,{"disambiguationData":[TD([[makeQuery(id+"F0.imprint","IMPRINT",EDGE,{"derivedFrom":sQuery(id+"F0.wireOp",EDGE,"E24")}),-1.0]])]});
            var Q5;
            {var subQ2=sQuery(id+"F0.wireOp",EDGE,"E31");Q5=makeQuery(id+"F0.imprint","IMPRINT",FACE,{"disambiguationData":[TD([[makeQuery(id+"F0.imprint","IMPRINT",EDGE,{"derivedFrom":subQ2}),-1.0]])]});}
            var Q6;
            Q6=makeQuery(id+"F0.imprint","IMPRINT",FACE,{"disambiguationData":[TD([[makeQuery(id+"F0.imprint","IMPRINT",EDGE,{"derivedFrom":sQuery(id+"F0.wireOp",EDGE,"E20")}),-1.0]])]});
            var Q7;
            {var subQ0=sQuery(id+"F0.wireOp",EDGE,"E227");Q7=makeQuery(id+"F0.imprint","IMPRINT",FACE,{"disambiguationData":[TD([[makeQuery(id+"F0.imprint","IMPRINT",EDGE,{"derivedFrom":subQ0}),-1.0]])]});}
            extrude(context, id + "F10", {"entities" : qUnion([Q0, Q1, Q2, Q3, Q4, Q5, Q6, Q7]), "operationType" : NewBodyOperationType.ADD, "depth" : 304.8 * mm});
        }
        {
            var Q0;
            {var subQ2=sQuery(id+"F0.wireOp",EDGE,"E156");Q0=makeQuery(id+"F0.imprint","IMPRINT",FACE,{"disambiguationData":[TD([[makeQuery(id+"F0.imprint","IMPRINT",EDGE,{"derivedFrom":subQ2}),-1.0]])]});}
            var Q1;
            Q1=makeQuery(id+"F0.imprint","IMPRINT",FACE,{"disambiguationData":[TD([[makeQuery(id+"F0.imprint","IMPRINT",EDGE,{"derivedFrom":sQuery(id+"F0.wireOp",EDGE,"E154.2.0.1")}),1.0]])]});
            var Q2;
            Q2=makeQuery(id+"F0.imprint","IMPRINT",FACE,{"disambiguationData":[TD([[makeQuery(id+"F0.imprint","IMPRINT",EDGE,{"derivedFrom":sQuery(id+"F0.wireOp",EDGE,"E154.3.0.1")}),1.0]])]});
            extrude(context, id + "F11", {"entities" : qUnion([Q0, Q1, Q2]), "depth" : 4876.8 * mm});
        }
    });
